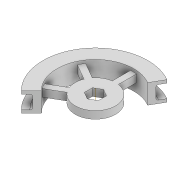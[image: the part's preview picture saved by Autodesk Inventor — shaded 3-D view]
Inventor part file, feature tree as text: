
AUTODESK INVENTOR PART (.ipt)
format: ipt  version: 2022 (Build 260153000, 153)  size: 198,656 bytes
history: native  units: mm
features: extrude x7, sketch x7, projected_geometry x4, fillet x1
ambient origin geometry x8: Origin, YZ Plane, XZ Plane, XY Plane, X Axis, Y Axis, Z Axis, Center Point
bodies: Solid1 (feature_tree)
feature tree (19):
  extrude  "Extrusion1"  Depth=44.0mm
  extrude  "Extrusion4"  Depth=3.7mm
  extrude  "Extrusion10"  Depth=1.5mm TaperAngle=0.0deg
  extrude  "Extrusion5"  Depth=3.0mm
  extrude  "Extrusion7"  Depth=1.5mm
  extrude  "Extrusion8"  Depth=10.0mm TaperAngle=0.0deg
  fillet  "Fillet1"  Radius=7.0mm
  extrude  "Extrusion9"  Depth=1.0mm
  sketch  "Sketch1"  dims[d0=4.1mm d1=44.0mm]
  sketch  "Sketch5"  dims[d2=3.7mm d3=0.0mm d11=4.0mm]
  projected_geometry  "Projected Loop4"
  sketch  "Sketch6"  dims[d12=1.5mm d13=0.0mm d15=1.5mm d16=0.0mm]
  projected_geometry  "Projected Loop5"
  sketch  "Sketch7"  dims[d17=3.0mm d19=20.0mm]
  projected_geometry  "Projected Loop6"
  sketch  "Sketch8"  dims[d20=3.0mm d21=1.5mm]
  sketch  "Sketch9"  dims[d24=60.0mm d26=360.0deg d28=10.0mm d29=0.0mm d30=7.0mm]
  sketch  "Sketch11"  dims[d31=10.0mm d32=0.0mm d33=1.0mm d34=150.0deg d35=45.0deg d36=10.0mm d37=0.0mm d38=3.0mm d39=3.0mm d40=0.0mm d41=20.0mm]
  projected_geometry  "Projected Loop7"
